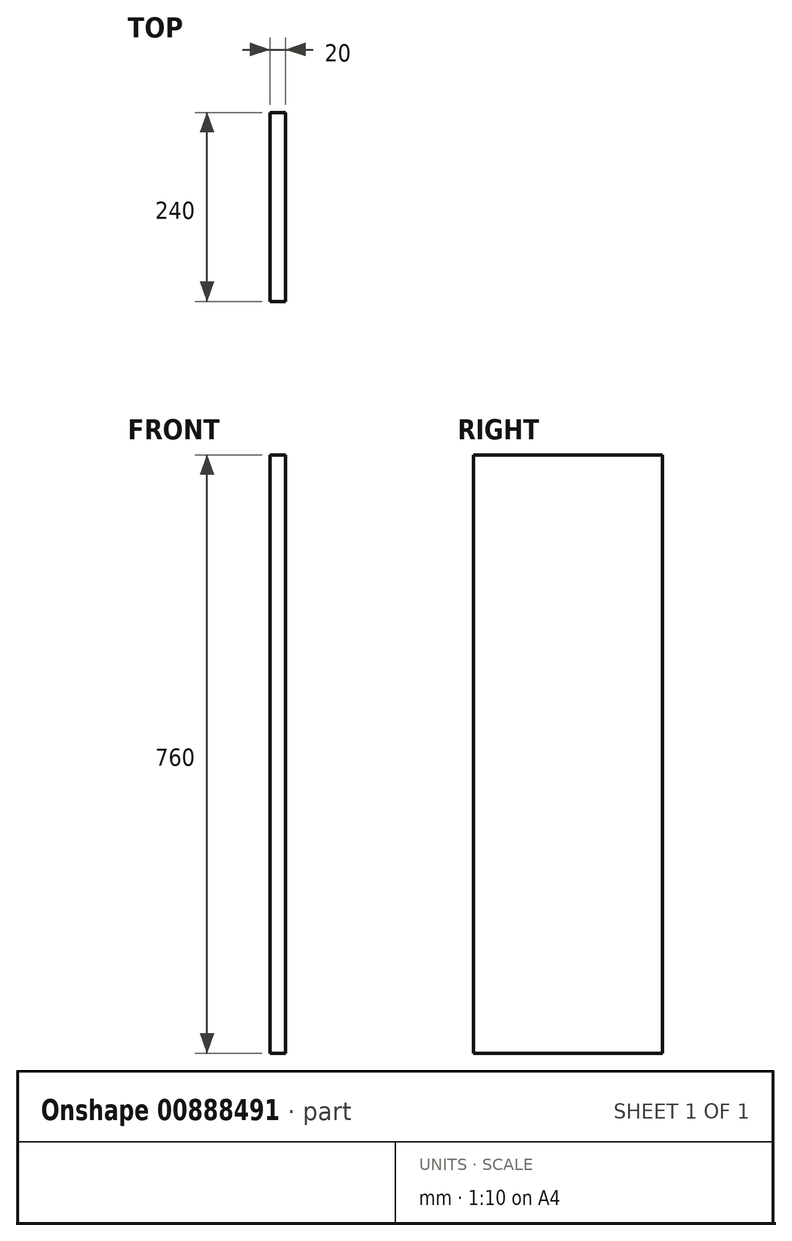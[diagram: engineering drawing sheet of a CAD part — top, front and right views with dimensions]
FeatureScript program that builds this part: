
annotation { "Feature Type Name" : "Feature", "Feature Type Description" : "" }
export const myFeature = defineFeature(function(context is Context, id is Id, definition is map)
    precondition{}
    {
        {
            var Q0;
            Q0=qCreatedBy(makeId("Right.planeOp"),FACE);
            var sketch = newSketch(context, id + "F0", { "sketchPlane" : qUnion([Q0])});
            skLineSegment(sketch, "E0.bottom", {"start": v(120, 380) * mm, "end": v(-120, 380) * mm});
            skLineSegment(sketch, "E0.top", {"start": v(120, -380) * mm, "end": v(-120, -380) * mm});
            skLineSegment(sketch, "E0.left", {"start": v(120, 380) * mm, "end": v(120, -380) * mm});
            skLineSegment(sketch, "E0.right", {"start": v(-120, 380) * mm, "end": v(-120, -380) * mm});
            skPoint(sketch, "E0.middle", {"position": v(0, 0) * mm});
            skSolve(sketch);
        }
        {
            var Q0;
            Q0 = qSketchRegion(id + "F0", true);
            extrude(context, id + "F1", {"entities" : qUnion([Q0]), "depth" : 20 * mm, "offsetDistance" : 25 * mm});
        }
    });
